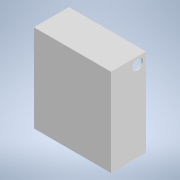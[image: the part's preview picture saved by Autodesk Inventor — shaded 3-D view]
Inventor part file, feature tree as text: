
AUTODESK INVENTOR PART (.ipt)
format: ipt  version: 2020 (Build 240168000, 168)  size: 120,320 bytes
history: native  units: mm
features: extrude x4, sketch x4
ambient origin geometry x8: Origin, YZ Plane, XZ Plane, XY Plane, X Axis, Y Axis, Z Axis, Center Point
bodies: Solid1 (feature_tree)
feature tree (8):
  extrude  "Extrusion1"  Depth=250.0mm
  extrude  "Extrusion2"  Depth=210.0mm
  extrude  "Extrusion3"  Depth=95.0mm TaperAngle=0.0deg
  extrude  "Extrusion4"  Depth=10.0mm
  sketch  "Sketch1"  dims[d0=220.0mm d1=250.0mm]
  sketch  "Sketch2"  dims[d2=100.0mm d3=0.0mm d4=210.0mm]
  sketch  "Sketch3"  dims[d5=240.0mm d6=95.0mm d7=0.0mm]
  sketch  "Sketch4"  dims[d8=5.0mm d9=30.0mm d10=20.0mm d11=45.0mm d12=0.0mm d13=5.0mm d14=10.0mm d15=0.0mm]
